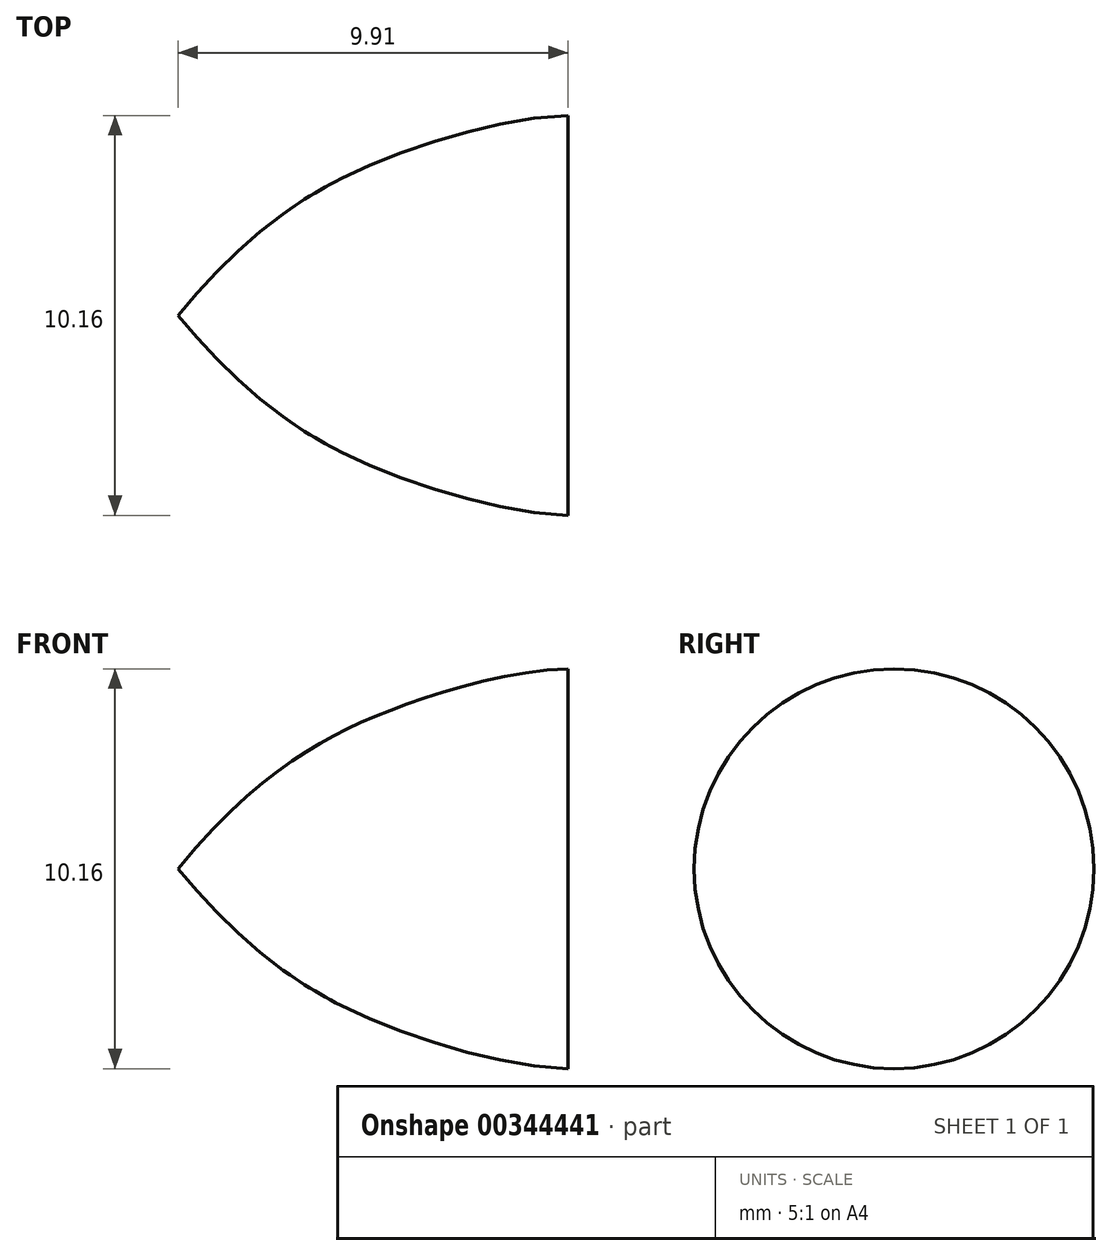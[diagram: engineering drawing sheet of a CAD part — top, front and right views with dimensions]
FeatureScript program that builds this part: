
annotation { "Feature Type Name" : "Feature", "Feature Type Description" : "" }
export const myFeature = defineFeature(function(context is Context, id is Id, definition is map)
    precondition{}
    {
        {
            var Q0;
            Q0=qCreatedBy(makeId("Front.planeOp"),FACE);
            var sketch = newSketch(context, id + "F0", { "sketchPlane" : qUnion([Q0])});
            skLineSegment(sketch, "E0", {"start": v(0, 0) * mm, "end": v(9.9, 0) * mm});
            skLineSegment(sketch, "E1", {"start": v(9.9, 0) * mm, "end": v(9.9, 5.08) * mm});
            skFitSpline(sketch, "E2", {"points": [v(0, 0) * mm, v(3.43, 3.08) * mm, v(5.73, 4.15) * mm, v(9.9, 5.08) * mm], "startDerivative": vector(10.86, 13.23) * mm, "endDerivative": vector(12.24, 0.4) * mm});
            skLineSegment(sketch, "E3", {"start": v(-0.63, 0) * mm, "end": v(14.2, 0) * mm});
            skSolve(sketch);
        }
        {
            var Q0;
            Q0 = qSketchRegion(id + "F0", true);
            var Q1;
            Q1=sQuery(id+"F0.wireOp",EDGE,"E3");
            revolve(context, id + "F1", {"entities" : qUnion([Q0]), "axis" : qUnion([Q1]), "revolveType" : RevolveType.FULL});
        }
    });
